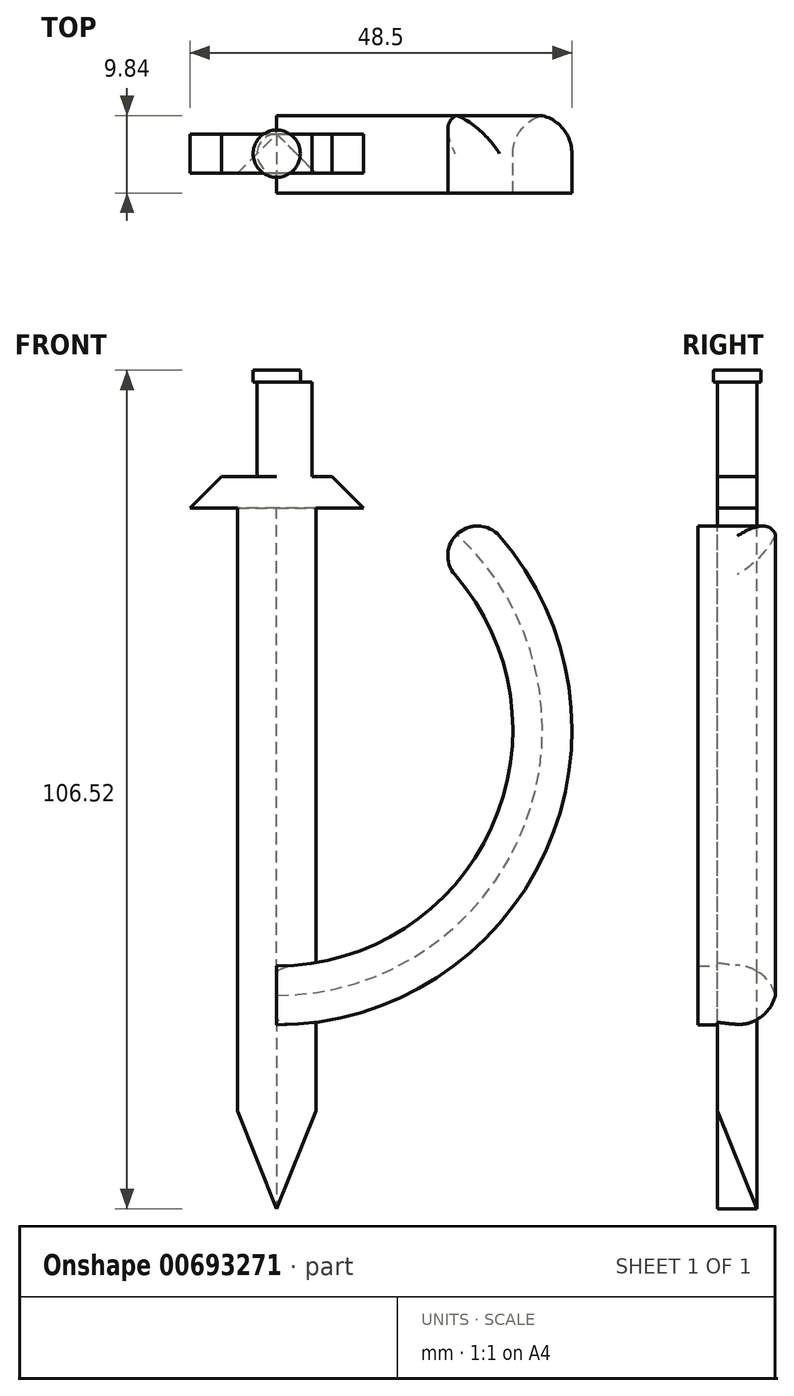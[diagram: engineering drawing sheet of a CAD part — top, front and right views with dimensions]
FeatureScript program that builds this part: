
annotation { "Feature Type Name" : "Feature", "Feature Type Description" : "" }
export const myFeature = defineFeature(function(context is Context, id is Id, definition is map)
    precondition{}
    {
        {
            var Q0;
            Q0=qCreatedBy(makeId("Front.planeOp"),FACE);
            var sketch = newSketch(context, id + "F0", { "sketchPlane" : qUnion([Q0])});
            skLineSegment(sketch, "E0.bottom", {"start": v(-37.5, 65) * mm, "end": v(37.5, 65) * mm, "construction": true});
            skLineSegment(sketch, "E0.top", {"start": v(-37.5, -65) * mm, "end": v(37.5, -65) * mm, "construction": true});
            skLineSegment(sketch, "E0.left", {"start": v(-37.5, 65) * mm, "end": v(-37.5, -65) * mm, "construction": true});
            skLineSegment(sketch, "E0.right", {"start": v(37.5, 65) * mm, "end": v(37.5, -65) * mm, "construction": true});
            skPoint(sketch, "E0.middle", {"position": v(0, 0) * mm});
            skLineSegment(sketch, "E1", {"start": v(0, 65) * mm, "end": v(0, -65) * mm, "construction": true});
            skArc(sketch, "E2", {"start": v(0, -30) * mm, "mid": v(27.3, -12.43) * mm, "end": v(22.63, 19.7) * mm});
            skArc(sketch, "E3", {"start": v(0, -37.5) * mm, "mid": v(34.13, -15.54) * mm, "end": v(28.28, 24.62) * mm});
            skLineSegment(sketch, "E4", {"start": v(37.5, 0) * mm, "end": v(37.5, 65) * mm, "construction": true});
            skLineSegment(sketch, "E5", {"start": v(37.5, 32.5) * mm, "end": v(0, 0) * mm, "construction": true});
            skArc(sketch, "E6", {"start": v(28.34, 24.56) * mm, "mid": v(23.02, 24.97) * mm, "end": v(22.67, 19.65) * mm});
            skArc(sketch, "E7.MirrorCS", {"start": v(-28.34, 24.56) * mm, "mid": v(-23.02, 24.97) * mm, "end": v(-22.67, 19.65) * mm});
            skArc(sketch, "E8.MirrorCS", {"start": v(0, -30) * mm, "mid": v(-27.3, -12.43) * mm, "end": v(-22.63, 19.7) * mm});
            skArc(sketch, "E9.MirrorCS", {"start": v(0, -37.5) * mm, "mid": v(-34.13, -15.54) * mm, "end": v(-28.28, 24.62) * mm});
            skLineSegment(sketch, "E10", {"start": v(0, -65) * mm, "end": v(0, 65) * mm});
            skSolve(sketch);
        }
        {
            var Q0;
            {var subQ3=sQuery(id+"F0.wireOp",EDGE,"E7.MirrorCS");var subQ5=sQuery(id+"F0.wireOp",EDGE,"E8.MirrorCS");var subQ7=makeQuery(id+"F0.imprint","INTERSECT",VERTEX,{"disambiguationData":[OD(1.0)],"derivedFrom":[subQ3,subQ5]});Q0=makeQuery(id+"F0.imprint","IMPRINT",FACE,{"disambiguationData":[TD([[makeQuery(id+"F0.imprint","IMPRINT",EDGE,{"disambiguationData":[TD([[subQ7,1.0]])],"derivedFrom":subQ3}),-1.0]])]});}
            var Q1;
            {var subQ0=sQuery(id+"F0.wireOp",EDGE,"E6");var subQ5=sQuery(id+"F0.wireOp",EDGE,"E2");var subQ8=makeQuery(id+"F0.imprint","INTERSECT",VERTEX,{"disambiguationData":[OD(0.0)],"derivedFrom":[subQ5,subQ0]});Q1=makeQuery(id+"F0.imprint","IMPRINT",FACE,{"disambiguationData":[TD([[makeQuery(id+"F0.imprint","IMPRINT",EDGE,{"disambiguationData":[TD([[subQ8,1.0]])],"derivedFrom":subQ5}),-1.0]])]});}
            extrude(context, id + "F1", {"entities" : qUnion([Q0, Q1]), "endBound" : BoundingType.SYMMETRIC, "depth" : 10 * mm, "offsetDistance" : 25 * mm});
        }
        {
            var Q0;
            Q0=makeQuery(id+"F1.opExtrude","CAP_EDGE",EDGE,{"disambiguationData":[OSD([sQuery(id+"F0.wireOp",EDGE,"E3"),sQuery(id+"F0.wireOp",EDGE,"E9.MirrorCS")])],"isStart":true});
            var Q1;
            Q1=makeQuery(id+"F1.opExtrude","CAP_EDGE",EDGE,{"disambiguationData":[OSD([sQuery(id+"F0.wireOp",EDGE,"E2"),sQuery(id+"F0.wireOp",EDGE,"E8.MirrorCS")])],"isStart":true});
            fillet(context, id + "F2", {"entities" : qUnion([Q0, Q1]), "tangentPropagation" : true, "radius" : 5 * mm, "defaultsChanged" : false, "vertexSettings" : [], "allowEdgeOverflow" : false});
        }
        {
            var Q0;
            Q0=qCreatedBy(makeId("Front.planeOp"),FACE);
            var sketch = newSketch(context, id + "F3", { "sketchPlane" : qUnion([Q0])});
            skLineSegment(sketch, "E11", {"start": v(0, 44.18) * mm, "end": v(0, 41.18) * mm, "construction": true});
            skLineSegment(sketch, "E12", {"start": v(0, 44.18) * mm, "end": v(-12, 44.18) * mm, "construction": true});
            skLineSegment(sketch, "E13", {"start": v(-12, 44.18) * mm, "end": v(0, 44.18) * mm, "construction": true});
            skLineSegment(sketch, "E14", {"start": v(0, 44.18) * mm, "end": v(12, 44.18) * mm, "construction": true});
            skLineSegment(sketch, "E15", {"start": v(12, 44.18) * mm, "end": v(12, -60.84) * mm, "construction": true});
            skLineSegment(sketch, "E16", {"start": v(12, -60.84) * mm, "end": v(0, -60.84) * mm, "construction": true});
            skLineSegment(sketch, "E17", {"start": v(-12, -60.84) * mm, "end": v(0, -60.84) * mm, "construction": true});
            skLineSegment(sketch, "E18", {"start": v(-12, -60.84) * mm, "end": v(-12, 44.18) * mm, "construction": true});
            skLineSegment(sketch, "E19.bottom", {"start": v(6, -60.84) * mm, "end": v(-6, -60.84) * mm, "construction": true});
            skLineSegment(sketch, "E19.top", {"start": v(6, -60.84) * mm, "end": v(-6, -60.84) * mm, "construction": true});
            skLineSegment(sketch, "E19.left", {"start": v(6, -60.84) * mm, "end": v(6, -60.84) * mm});
            skLineSegment(sketch, "E19.right", {"start": v(-6, -60.84) * mm, "end": v(-6, -60.84) * mm});
            skLineSegment(sketch, "E20.bottom", {"start": v(-6, -60.84) * mm, "end": v(6, -60.84) * mm, "construction": true});
            skLineSegment(sketch, "E20.top", {"start": v(-6, 44.18) * mm, "end": v(6, 44.18) * mm, "construction": true});
            skLineSegment(sketch, "E20.left", {"start": v(-6, -45.97) * mm, "end": v(-6, 24.56) * mm, "construction": true});
            skLineSegment(sketch, "E20.right", {"start": v(6, -60.84) * mm, "end": v(6, 44.18) * mm, "construction": true});
            skLineSegment(sketch, "E21", {"start": v(0, -60.84) * mm, "end": v(-6, -45.97) * mm});
            skLineSegment(sketch, "E22", {"start": v(-6, -45.97) * mm, "end": v(-6, 24.56) * mm});
            skLineSegment(sketch, "E23", {"start": v(-28.34, 24.56) * mm, "end": v(-12, 24.56) * mm, "construction": true});
            skLineSegment(sketch, "E24", {"start": v(-6, 28.18) * mm, "end": v(-12, 28.18) * mm});
            skLineSegment(sketch, "E25", {"start": v(-12, 28.18) * mm, "end": v(-12, 24.56) * mm});
            skLineSegment(sketch, "E26.trimOffspring", {"start": v(-6, 32.18) * mm, "end": v(-6, 44.18) * mm});
            skLineSegment(sketch, "E27.trimOffspring", {"start": v(-6, 32.18) * mm, "end": v(-6, 44.18) * mm, "construction": true});
            skLineSegment(sketch, "E28", {"start": v(-6, 32.18) * mm, "end": v(0, 32.18) * mm});
            skLineSegment(sketch, "E29", {"start": v(-6, 32.18) * mm, "end": v(-12, 32.18) * mm});
            skLineSegment(sketch, "E30", {"start": v(-12, 32.18) * mm, "end": v(-12, 28.18) * mm});
            skLineSegment(sketch, "E31", {"start": v(-6, 24.56) * mm, "end": v(-6, 28.18) * mm});
            skLineSegment(sketch, "E32", {"start": v(0, 32.18) * mm, "end": v(-3, 32.18) * mm, "construction": true});
            skLineSegment(sketch, "E33", {"start": v(-3, 41.18) * mm, "end": v(-3, 44.18) * mm, "construction": true});
            skLineSegment(sketch, "E34", {"start": v(-6, 32.18) * mm, "end": v(-3, 32.18) * mm, "construction": true});
            skLineSegment(sketch, "E35", {"start": v(-4.5, 32.18) * mm, "end": v(-4.5, 41.18) * mm});
            skLineSegment(sketch, "E36", {"start": v(-4.5, 41.18) * mm, "end": v(-3, 41.18) * mm});
            skPoint(sketch, "E37.orphan", {"position": v(-3, 38.18) * mm});
            skLineSegment(sketch, "E38.MirrorCS", {"start": v(4.5, 41.18) * mm, "end": v(3, 41.18) * mm});
            skLineSegment(sketch, "E39.MirrorCS", {"start": v(4.5, 32.18) * mm, "end": v(4.5, 41.18) * mm});
            skLineSegment(sketch, "E40.MirrorCS", {"start": v(6, 32.18) * mm, "end": v(12, 32.18) * mm});
            skLineSegment(sketch, "E41.MirrorCS", {"start": v(6, 28.18) * mm, "end": v(12, 28.18) * mm});
            skLineSegment(sketch, "E42.MirrorCS", {"start": v(6, 32.18) * mm, "end": v(0, 32.18) * mm});
            skLineSegment(sketch, "E43.MirrorCS", {"start": v(6, -45.97) * mm, "end": v(6, 24.56) * mm});
            skLineSegment(sketch, "E44.MirrorCS", {"start": v(6, 24.56) * mm, "end": v(6, 28.18) * mm});
            skLineSegment(sketch, "E45.MirrorCS", {"start": v(0, -60.84) * mm, "end": v(6, -45.97) * mm});
            skLineSegment(sketch, "E46.MirrorCS", {"start": v(12, 32.18) * mm, "end": v(12, 28.18) * mm});
            skLineSegment(sketch, "E47.bottom", {"start": v(4.5, 32.18) * mm, "end": v(-4.5, 32.18) * mm});
            skLineSegment(sketch, "E47.top", {"start": v(4.5, 32.18) * mm, "end": v(-4.5, 32.18) * mm});
            skLineSegment(sketch, "E47.left", {"start": v(4.5, 32.18) * mm, "end": v(4.5, 32.18) * mm});
            skLineSegment(sketch, "E47.right", {"start": v(-4.5, 32.18) * mm, "end": v(-4.5, 32.18) * mm});
            skLineSegment(sketch, "E48.top", {"start": v(-4.5, 44.18) * mm, "end": v(-4.5, 44.18) * mm});
            skLineSegment(sketch, "E48.left", {"start": v(-4.5, 32.18) * mm, "end": v(-4.5, 44.18) * mm});
            skLineSegment(sketch, "E48.right", {"start": v(-4.5, 32.18) * mm, "end": v(-4.5, 44.18) * mm});
            skLineSegment(sketch, "E49.top", {"start": v(4.5, 44.18) * mm, "end": v(4.5, 44.18) * mm});
            skLineSegment(sketch, "E49.left", {"start": v(4.5, 32.18) * mm, "end": v(4.5, 44.18) * mm});
            skLineSegment(sketch, "E49.right", {"start": v(4.5, 32.18) * mm, "end": v(4.5, 44.18) * mm});
            skLineSegment(sketch, "E50", {"start": v(4.5, 44.18) * mm, "end": v(-4.5, 44.18) * mm});
            skPoint(sketch, "E51.end.orphan", {"position": v(0, 41.18) * mm});
            skPoint(sketch, "E52.MirrorCS.start.orphan", {"position": v(3, 41.18) * mm});
            skPoint(sketch, "E53.start.orphan", {"position": v(-3, 28.18) * mm});
            skLineSegment(sketch, "E54", {"start": v(6, 28.18) * mm, "end": v(-6, 28.18) * mm});
            skLineSegment(sketch, "E55.trimOffspring", {"start": v(0, 41.18) * mm, "end": v(0, 44.18) * mm});
            skPoint(sketch, "E56.end.orphan", {"position": v(0, 24.56) * mm});
            skPoint(sketch, "E57.trimOffspring.start.orphan", {"position": v(0, 28.18) * mm});
            skSolve(sketch);
        }
        {
            var Q0;
            Q0=makeQuery(id+"F3.imprint","IMPRINT",FACE,{"disambiguationData":[TD([[makeQuery(id+"F3.imprint","IMPRINT",EDGE,{"derivedFrom":sQuery(id+"F3.wireOp",EDGE,"E24")}),-1.0]])]});
            var Q1;
            Q1=makeQuery(id+"F3.imprint","IMPRINT",FACE,{"disambiguationData":[TD([[makeQuery(id+"F3.imprint","IMPRINT",EDGE,{"derivedFrom":sQuery(id+"F3.wireOp",EDGE,"E21")}),-1.0]])]});
            extrude(context, id + "F4", {"entities" : qUnion([Q0, Q1]), "operationType" : NewBodyOperationType.ADD, "endBound" : BoundingType.SYMMETRIC, "oppositeDirection" : true, "depth" : 5 * mm, "offsetDistance" : 25 * mm});
        }
        {
            var Q0;
            {var subQ7=sQuery(id+"F3.wireOp",EDGE,"E35");Q0=makeQuery(id+"F3.imprint","IMPRINT",FACE,{"disambiguationData":[TD([[makeQuery(id+"F3.imprint","IMPRINT",EDGE,{"derivedFrom":subQ7}),-1.0]])]});}
            extrude(context, id + "F5", {"entities" : qUnion([Q0]), "operationType" : NewBodyOperationType.ADD, "endBound" : BoundingType.SYMMETRIC, "oppositeDirection" : true, "depth" : 5 * mm, "offsetDistance" : 25 * mm});
        }
        {
            var Q0;
            Q0=makeQuery(id+"F4.opExtrude","CAP_EDGE",EDGE,{"disambiguationData":[OSD([sQuery(id+"F3.wireOp",EDGE,"E22"),sQuery(id+"F3.wireOp",EDGE,"E31")])],"isStart":false});
            var Q1;
            Q1=makeQuery(id+"F4.opExtrude","CAP_EDGE",EDGE,{"disambiguationData":[OSD([sQuery(id+"F3.wireOp",EDGE,"E43.MirrorCS"),sQuery(id+"F3.wireOp",EDGE,"E44.MirrorCS")])],"isStart":false});
            chamfer(context, id + "F6", {"entities" : qUnion([Q0, Q1]), "width" : 6 * mm, "tangentPropagation" : true});
        }
        {
            var Q0;
            Q0=makeQuery(id+"F5.opExtrude","SWEPT_FACE",FACE,{"disambiguationData":[OSD([sQuery(id+"F3.wireOp",EDGE,"E50")])]});
            var sketch = newSketch(context, id + "F7", { "sketchPlane" : qUnion([Q0])});
            skCircle(sketch, "E58", {"center": v(0, 0) * mm, "radius": 2.5 * mm});
            skSolve(sketch);
        }
        {
            var Q0;
            Q0=makeQuery(id+"F4.opExtrude","SWEPT_EDGE",EDGE,{"disambiguationData":[OSD([sQuery(id+"F3.wireOp",EDGE,"E29"),sQuery(id+"F3.wireOp",EDGE,"E30")])]});
            var Q1;
            Q1=makeQuery(id+"F4.opExtrude","SWEPT_EDGE",EDGE,{"disambiguationData":[OSD([sQuery(id+"F3.wireOp",EDGE,"E40.MirrorCS"),sQuery(id+"F3.wireOp",EDGE,"E46.MirrorCS")])]});
            chamfer(context, id + "F8", {"entities" : qUnion([Q0, Q1]), "width" : 5 * mm, "tangentPropagation" : true});
        }
        {
            var Q0;
            {var subQ0=sQuery(id+"F3.wireOp",EDGE,"E50");Q0=makeQuery(id+"F7.imprint","IMPRINT",FACE,{"disambiguationData":[TD([[makeQuery(id+"F7.imprint","IMPRINT",EDGE,{"derivedFrom":makeQuery(id+"F5.opExtrude","CAP_EDGE",EDGE,{"disambiguationData":[OSD([subQ0])],"isStart":true})}),-1.0]])]});}
            var sketch = newSketch(context, id + "F9", { "sketchPlane" : qUnion([Q0])});
            skSolve(sketch);
        }
        {
            var Q0;
            {var subQ1=sQuery(id+"F3.wireOp",EDGE,"E50");var subQ6=makeQuery(id+"F5.opExtrude","SWEPT_EDGE",EDGE,{"disambiguationData":[OSD([sQuery(id+"F3.wireOp",EDGE,"E48.left"),subQ1])]});Q0=makeQuery(id+"F9.imprint","IMPRINT",FACE,{"disambiguationData":[TD([[makeQuery(id+"F9.imprint","IMPRINT",EDGE,{"derivedFrom":makeQuery(id+"F7.imprint","IMPRINT",EDGE,{"derivedFrom":subQ6})}),1.0]])]});}
            var Q1;
            {var subQ1=sQuery(id+"F3.wireOp",EDGE,"E50");var subQ6=makeQuery(id+"F5.opExtrude","SWEPT_EDGE",EDGE,{"disambiguationData":[OSD([sQuery(id+"F3.wireOp",EDGE,"E49.left"),subQ1])]});Q1=makeQuery(id+"F9.imprint","IMPRINT",FACE,{"disambiguationData":[TD([[makeQuery(id+"F9.imprint","IMPRINT",EDGE,{"derivedFrom":makeQuery(id+"F7.imprint","IMPRINT",EDGE,{"derivedFrom":subQ6})}),-1.0]])]});}
            extrude(context, id + "F10", {"entities" : qUnion([Q0, Q1]), "operationType" : NewBodyOperationType.REMOVE, "oppositeDirection" : true, "depth" : 12 * mm, "offsetDistance" : 25 * mm});
        }
        {
            var Q0;
            {var subQ0=sQuery(id+"F7.wireOp",EDGE,"E58");var subQ1=sQuery(id+"F3.wireOp",EDGE,"E50");var subQ2=makeQuery(id+"F7.imprint","INTERSECT",VERTEX,{"derivedFrom":[makeQuery(id+"F5.opExtrude","CAP_EDGE",EDGE,{"disambiguationData":[OSD([subQ1])],"isStart":true}),subQ0]});Q0=makeQuery(id+"F7.imprint","IMPRINT",FACE,{"disambiguationData":[TD([[makeQuery(id+"F7.imprint","IMPRINT",EDGE,{"disambiguationData":[TD([[subQ2,-1.0]])],"derivedFrom":subQ0}),-1.0]])]});}
            var sketch = newSketch(context, id + "F11", { "sketchPlane" : qUnion([Q0])});
            skCircle(sketch, "E59", {"center": v(0, 0) * mm, "radius": 3 * mm});
            skSolve(sketch);
        }
        {
            var Q0;
            Q0 = qSketchRegion(id + "F11", true);
            extrude(context, id + "F12", {"entities" : qUnion([Q0]), "operationType" : NewBodyOperationType.ADD, "depth" : 1.5 * mm, "offsetDistance" : 25 * mm});
        }
    });
